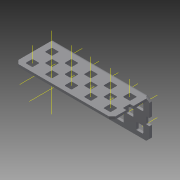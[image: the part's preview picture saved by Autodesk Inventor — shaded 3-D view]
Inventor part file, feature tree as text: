
AUTODESK INVENTOR PART (.ipt)
format: ipt  version: 2015 SP1 (Build 190203100, 203)  size: 1,938,432 bytes
history: native  units: in
note: dims shown in document units (in); Inventor stores cm internally (conversion verified against a paired STEP export)
features: other x35, pattern_linear x4, sheet_metal_op x1, extrude x1, imported_body x1, sketch x1
ambient origin geometry x8: Origin, YZ Plane, XZ Plane, XY Plane, X Axis, Y Axis, Z Axis, Center Point
bodies: Body1 (feature_tree)
feature tree (43):
  sheet_metal_op  "Fold1"
  other  "L-Channel"
  extrude  "length cut"  Depth=0.5in
  other  "top out axis"
  other  "top inner axis"
  other  "back out axis"
  other  "back inner axis"
  pattern_linear  "top outer axes"  Count1=2 Spacing1=0.5in
  pattern_linear  "top inner axes"  Spacing1=0.5in  [1 undecoded]
  pattern_linear  "back outer axes"  Count1=2 Spacing1=0.5in
  pattern_linear  "back inner axes"  Spacing1=0.5in  [1 undecoded]
  other  "right plane"
  imported_body  "Base1"
  sketch  "Sketch1"  dims[d1=0.0in d4=0.5in d5=0.7874in d7=0.5in d10=0.5in d13=0.5in d14=0.7874in d16=0.5in d19=0.5in d20=-2.5in d21=0.0in d22=0.0in d23=0.0in d24=0.0in d25=0.0in d26=0.0in]
  other  "Work Point1"
  other  "Work Point2"
  other  "Work Point3"
  other  "Work Point4"
  other  "Work Axis5"
  other  "Work Axis6"
  other  "Work Axis7"
  other  "Work Axis8"
  other  "Work Axis11"
  other  "Work Axis12"
  other  "Work Axis13"
  other  "Work Axis14"
  other  "Work Axis15"
  other  "Work Axis18"
  other  "Work Axis19"
  other  "Work Axis20"
  other  "Work Axis23"
  other  "Work Axis24"
  other  "Work Axis25"
  other  "Work Axis26"
  other  "Work Axis29"
  other  "Work Axis30"
  other  "Work Axis31"
  other  "Work Axis32"
  other  "Work Axis33"
  other  "Work Axis36"
  other  "Work Axis37"
  other  "Work Axis38"
  other  "left plane"
note: 2 required parameter values undecoded (feature->parameter linkage not recoverable at this tier; creation-order binding heuristic only, values carry confidence <= 0.55)
